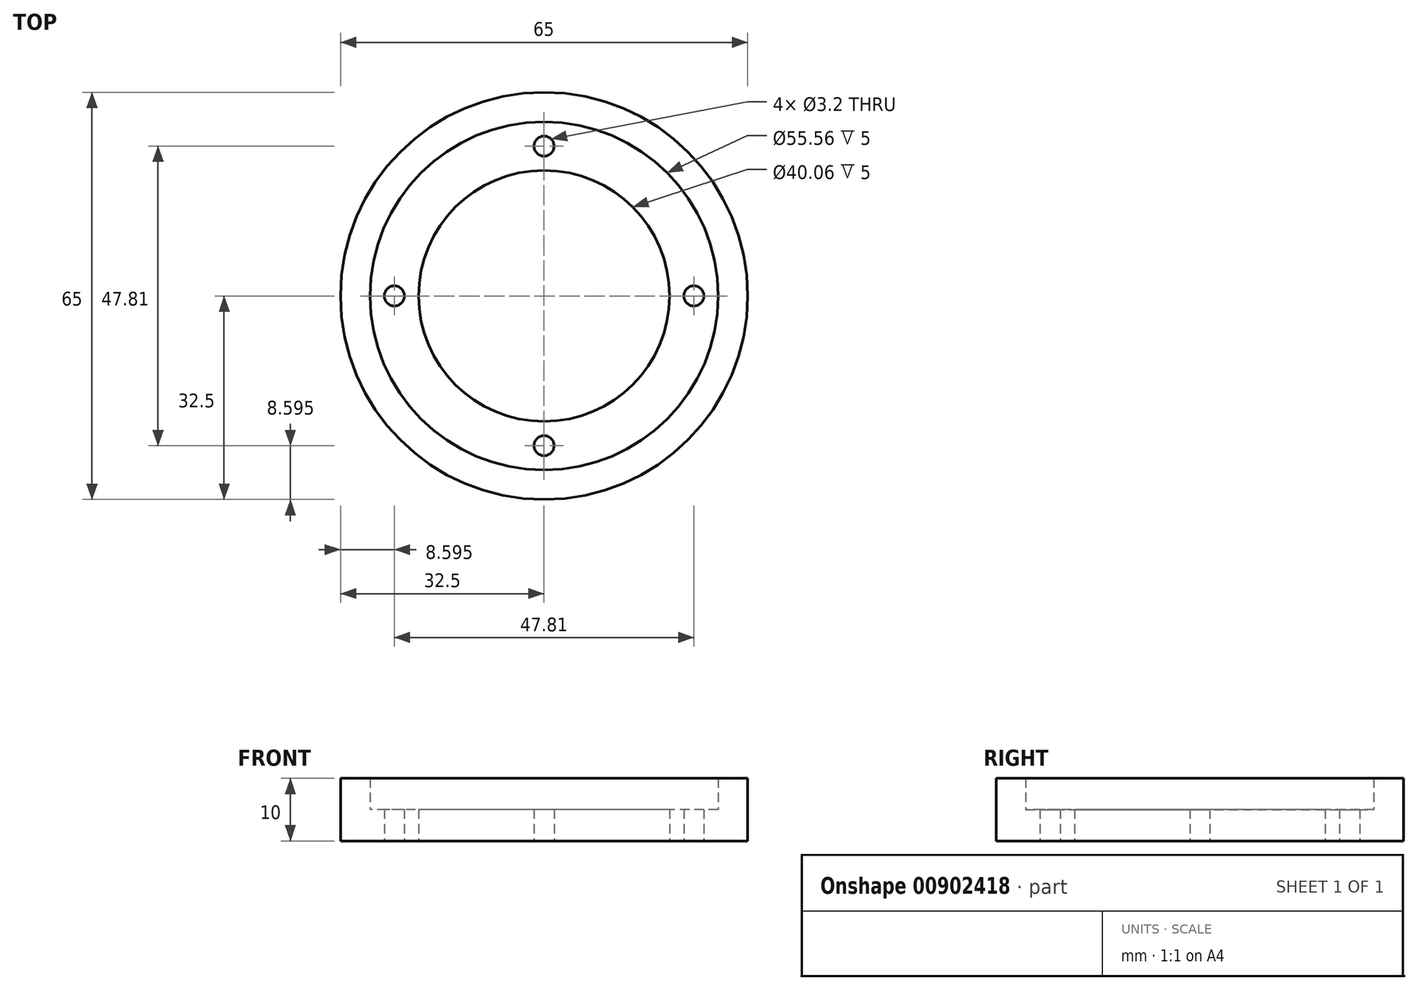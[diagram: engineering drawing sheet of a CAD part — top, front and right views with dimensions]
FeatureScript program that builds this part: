
annotation { "Feature Type Name" : "Feature", "Feature Type Description" : "" }
export const myFeature = defineFeature(function(context is Context, id is Id, definition is map)
    precondition{}
    {
        {
            var Q0;
            Q0=qCreatedBy(makeId("Top.planeOp"),FACE);
            var sketch = newSketch(context, id + "F0", { "sketchPlane" : qUnion([Q0])});
            skCircle(sketch, "E0", {"center": v(0, 0) * mm, "radius": 32.5 * mm});
            skCircle(sketch, "E1.0", {"center": v(0, 0) * mm, "radius": 27.78 * mm});
            skCircle(sketch, "E2.0", {"center": v(0, 0) * mm, "radius": 20.03 * mm});
            skLineSegment(sketch, "E3", {"start": v(0, 40.3) * mm, "end": v(0, -49.66) * mm, "construction": true});
            skLineSegment(sketch, "E4", {"start": v(-67.4, 0) * mm, "end": v(65.41, 0) * mm, "construction": true});
            skCircle(sketch, "E5", {"center": v(0, 23.9) * mm, "radius": 1.6 * mm});
            skCircle(sketch, "E6", {"center": v(23.9, 0) * mm, "radius": 1.6 * mm});
            skCircle(sketch, "E7.MirrorC", {"center": v(-23.9, 0) * mm, "radius": 1.6 * mm});
            skCircle(sketch, "E8.MirrorC", {"center": v(0, -23.9) * mm, "radius": 1.6 * mm});
            skSolve(sketch);
        }
        {
            var Q0;
            Q0=makeQuery(id+"F0.imprint","IMPRINT",FACE,{"disambiguationData":[TD([[makeQuery(id+"F0.imprint","IMPRINT",EDGE,{"derivedFrom":sQuery(id+"F0.wireOp",EDGE,"E0")}),1.0]])]});
            extrude(context, id + "F1", {"entities" : qUnion([Q0]), "depth" : 10 * mm, "offsetDistance" : 25 * mm});
        }
        {
            var Q0;
            Q0=makeQuery(id+"F0.imprint","IMPRINT",FACE,{"disambiguationData":[TD([[makeQuery(id+"F0.imprint","IMPRINT",EDGE,{"derivedFrom":sQuery(id+"F0.wireOp",EDGE,"E1.0")}),1.0]])]});
            extrude(context, id + "F2", {"entities" : qUnion([Q0]), "operationType" : NewBodyOperationType.ADD, "depth" : 5 * mm, "offsetDistance" : 25 * mm});
        }
    });
